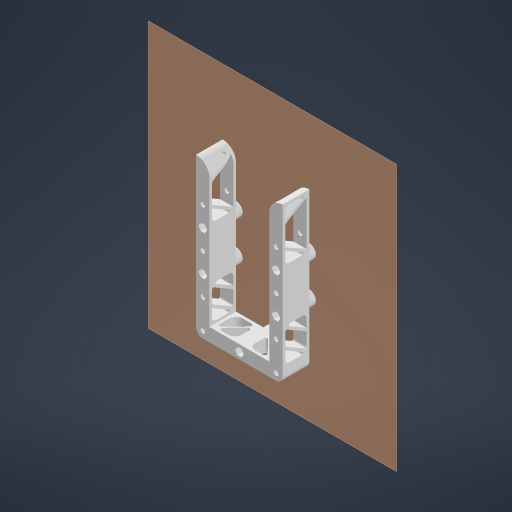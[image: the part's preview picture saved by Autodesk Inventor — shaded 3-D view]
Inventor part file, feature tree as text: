
AUTODESK INVENTOR PART (.ipt)
format: ipt  version: 2023 (Build 270158000, 158)  size: 623,104 bytes
history: native  units: mm
features: extrude x8, sketch x8, fillet x6, projected_geometry x5, plane x4, other x3, reference x1
ambient origin geometry x8: Origin, YZ Plane, XZ Plane, XY Plane, X Axis, Y Axis, Z Axis, Center Point
bodies: Body1 (feature_tree)
feature tree (35):
  plane  "Work Plane3"
  plane  "Work Plane4"
  plane  "Work Plane5"
  plane  "Work Plane6"
  extrude  "Extrusion3"  Depth=10.0mm
  extrude  "Extrusion4"  Depth=5.0mm TaperAngle=0.0deg
  extrude  "Extrusion5"  Depth=6.5mm
  fillet  "Fillet1"  Radius=60.0mm
  extrude  "Extrusion6"  Depth=60.0mm TaperAngle=360.0deg
  extrude  "Extrusion7"  Depth=60.0mm TaperAngle=360.0deg
  extrude  "Extrusion8"  Depth=5.0mm
  extrude  "Extrusion9"  Depth=45.0mm TaperAngle=0.0deg
  fillet  "Fillet2"  Radius=6.5mm
  fillet  "Fillet3"  Radius=60.0mm
  extrude  "Extrusion10"  Depth=1.0mm TaperAngle=360.0deg
  fillet  "Fillet4"  Radius=60.0mm
  fillet  "Fillet5"  Radius=3.0mm
  fillet  "Fillet6"  Radius=3.5mm
  sketch  "Sketch6"  dims[d38=10.0mm d39=6.5mm]
  reference  "Reference3"
  sketch  "Sketch7"  dims[d41=10.0mm d42=5.0mm d43=0.0mm]
  sketch  "Sketch8"  dims[d44=20.0mm d45=0.0mm d46=6.5mm d47=60.0mm d49=360.0deg]
  projected_geometry  "Projected Loop1"
  projected_geometry  "Projected Loop2"
  projected_geometry  "Projected Loop3"
  projected_geometry  "Projected Loop4"
  projected_geometry  "Projected Loop5"
  sketch  "Sketch9"  dims[d51=60.0mm d53=360.0deg d55=60.0mm d57=360.0deg]
  sketch  "Sketch10"  dims[d59=60.0mm d61=360.0deg d63=60.0mm d65=360.0deg]
  sketch  "Sketch11"  dims[d67=5.0mm d68=0.0mm d70=5.0mm]
  sketch  "Sketch12"  dims[d71=45.0mm d72=11.25mm d73=0.0mm d74=6.5mm d75=60.0mm d77=360.0deg]
  sketch  "Sketch13"  dims[d79=60.0mm d81=360.0deg d83=60.0mm d85=360.0deg d87=60.0mm d89=360.0deg d91=3.0mm d92=0.0mm d93=3.5mm d94=30.0mm d95=30.0mm d96=3.0mm d97=0.0mm d98=2.0mm d99=2.0mm d100=2.0mm d101=2.0mm d103=1.0mm d104=10.0mm d105=0.0mm d106=5.0mm d107=1.5mm d108=2.0mm d109=2.0mm d110=30.0deg d111=2.0mm d112=2.0mm d113=2.0mm d114=2.0mm d115=10.0mm d116=0.0mm d117=2.0mm d119=30.0deg d120=2.0mm d121=2.0mm d122=30.0deg d123=2.0mm d124=3.0mm d125=3.0mm d126=1.0mm d127=0.0mm d128=0.0mm d129=0.0mm]
  parser-record x1  (decoder bookkeeping rows leaked as tree rows — omitted from the tree; the rows remain in map.json)
  other  "total.iam"
  other  "bottom:1"
note: 1 file-system path scrubbed to <path> (originals preserved in map.json)
